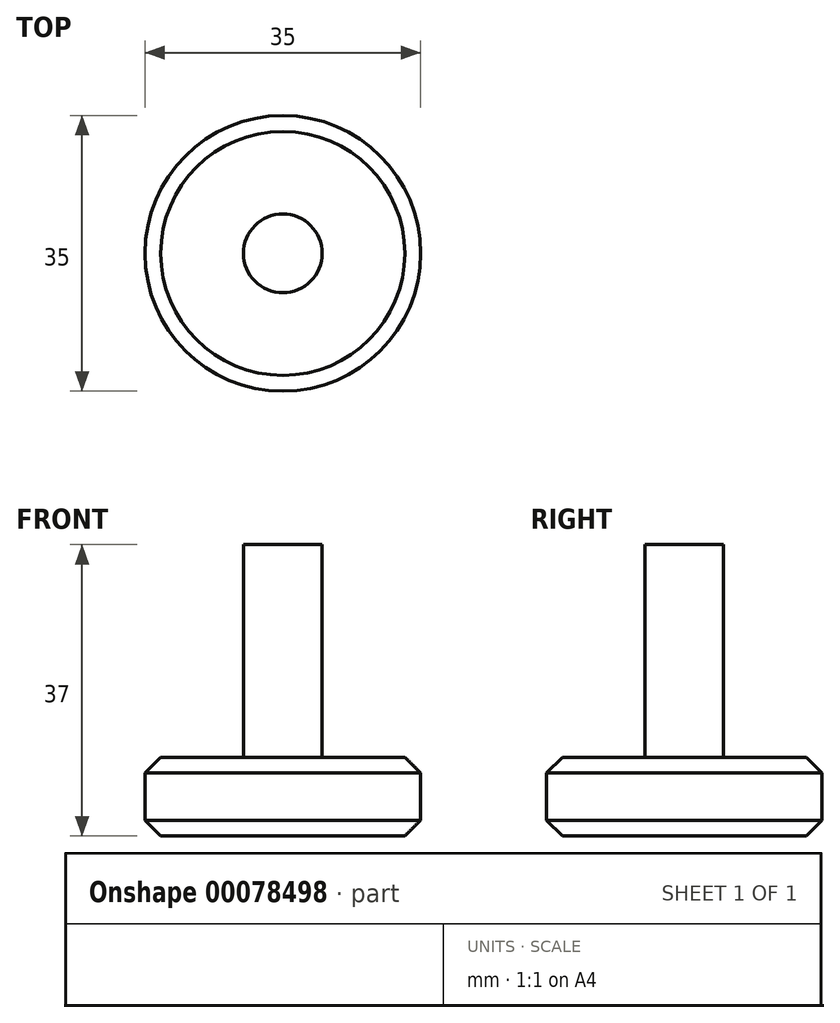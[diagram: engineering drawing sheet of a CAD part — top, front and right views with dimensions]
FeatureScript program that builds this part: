
annotation { "Feature Type Name" : "Feature", "Feature Type Description" : "" }
export const myFeature = defineFeature(function(context is Context, id is Id, definition is map)
    precondition{}
    {
        {
            var Q0;
            Q0=qCreatedBy(makeId("Top.planeOp"),FACE);
            var sketch = newSketch(context, id + "F0", { "sketchPlane" : qUnion([Q0])});
            skCircle(sketch, "E0", {"center": v(0, 0) * mm, "radius": 17.5 * mm});
            skSolve(sketch);
        }
        {
            var Q0;
            Q0 = qSketchRegion(id + "F0", true);
            extrude(context, id + "F1", {"entities" : qUnion([Q0]), "depth" : 10 * mm});
        }
        {
            var Q0;
            Q0=makeQuery(id+"F1.opExtrude","CAP_FACE",FACE,{"disambiguationData":[OSD([sQuery(id+"F0.wireOp",EDGE,"E0")])],"isStart":false});
            var sketch = newSketch(context, id + "F2", { "sketchPlane" : qUnion([Q0])});
            skCircle(sketch, "E1", {"center": v(0, 0) * mm, "radius": 5 * mm});
            skSolve(sketch);
        }
        {
            var Q0;
            Q0 = qSketchRegion(id + "F2", true);
            extrude(context, id + "F3", {"entities" : qUnion([Q0]), "operationType" : NewBodyOperationType.ADD, "depth" : 27 * mm});
        }
        {
            var Q0;
            Q0=makeQuery(id+"F1.opExtrude","CAP_EDGE",EDGE,{"disambiguationData":[OSD([sQuery(id+"F0.wireOp",EDGE,"E0")])],"isStart":false});
            var Q1;
            Q1=makeQuery(id+"F1.opExtrude","CAP_EDGE",EDGE,{"disambiguationData":[OSD([sQuery(id+"F0.wireOp",EDGE,"E0")])],"isStart":true});
            chamfer(context, id + "F4", {"entities" : qUnion([Q0, Q1]), "width" : 2 * mm, "tangentPropagation" : true});
        }
    });
